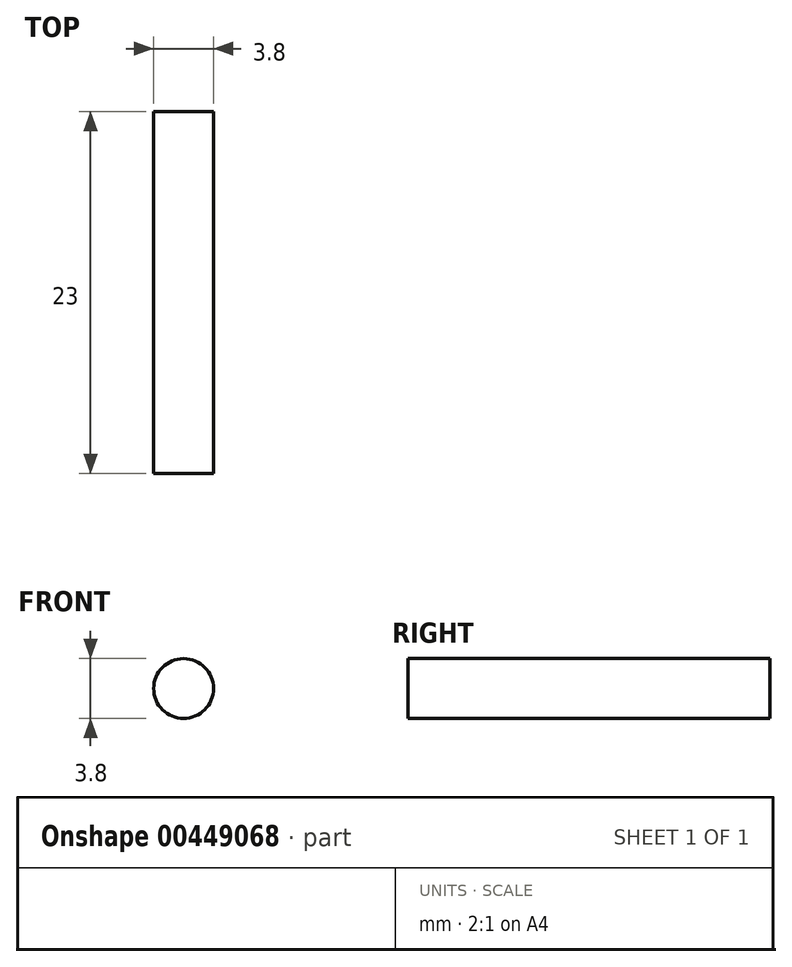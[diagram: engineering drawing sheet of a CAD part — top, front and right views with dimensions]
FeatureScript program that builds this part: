
annotation { "Feature Type Name" : "Feature", "Feature Type Description" : "" }
export const myFeature = defineFeature(function(context is Context, id is Id, definition is map)
    precondition{}
    {
        {
            var Q0;
            Q0=qCreatedBy(makeId("Front.planeOp"),FACE);
            var sketch = newSketch(context, id + "F0", { "sketchPlane" : qUnion([Q0])});
            skCircle(sketch, "E0", {"center": v(0, 0) * mm, "radius": 1.9 * mm});
            skSolve(sketch);
        }
        {
            var Q0;
            Q0=makeQuery(id+"F0.imprint","IMPRINT",FACE,{"disambiguationData":[TD([[makeQuery(id+"F0.imprint","IMPRINT",EDGE,{"derivedFrom":sQuery(id+"F0.wireOp",EDGE,"E0")}),1.0]])]});
            extrude(context, id + "F1", {"entities" : qUnion([Q0]), "depth" : (4 * 5 + 3 * 1) * mm});
        }
    });
